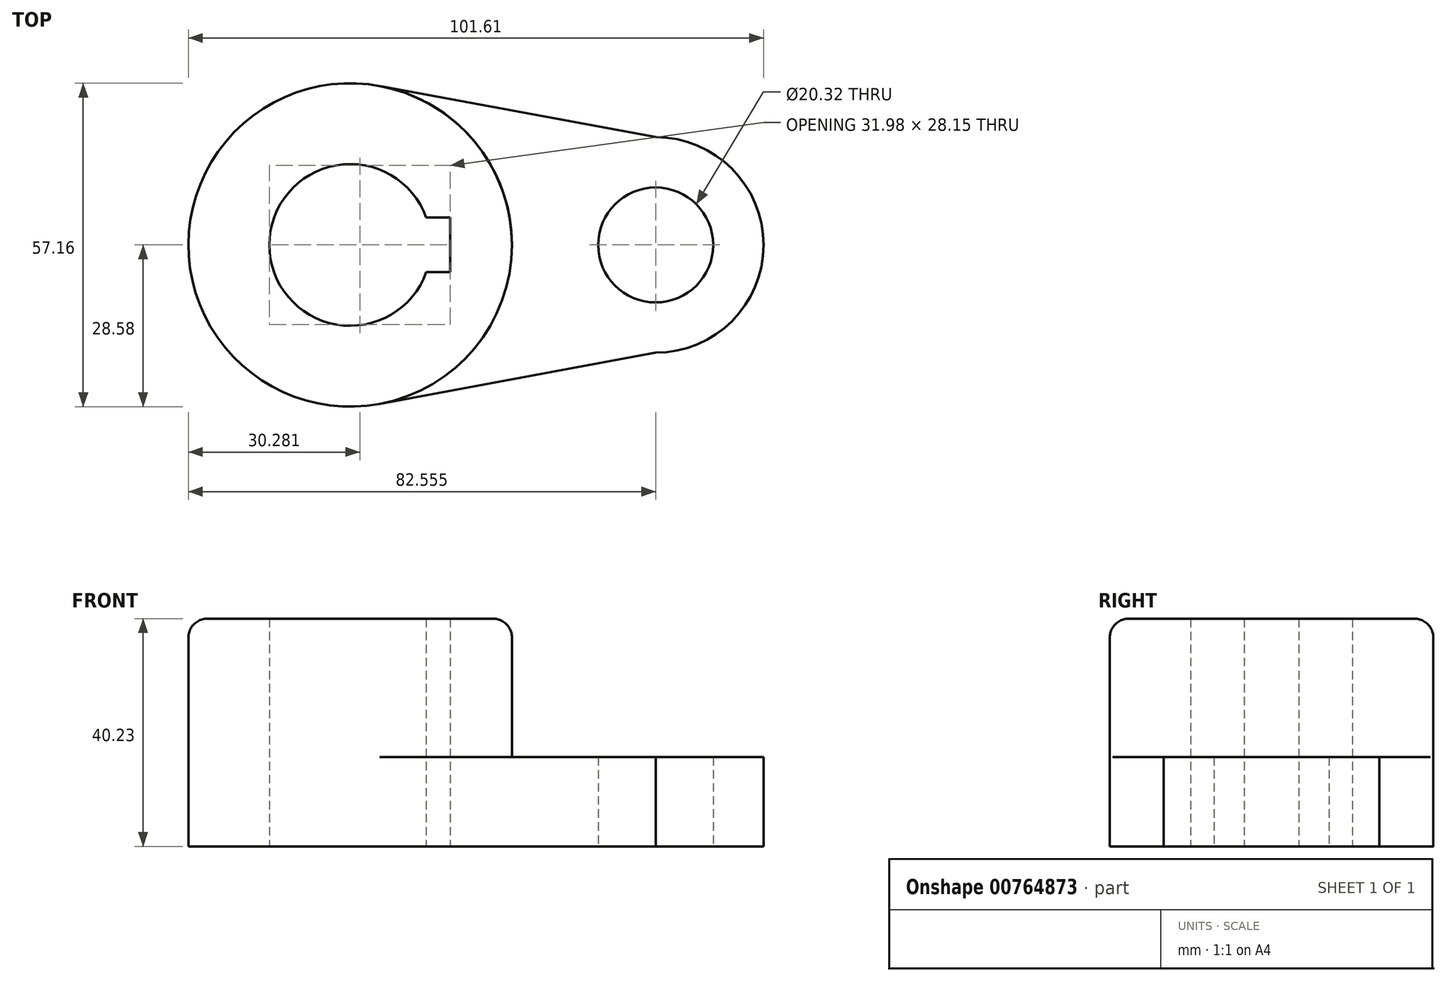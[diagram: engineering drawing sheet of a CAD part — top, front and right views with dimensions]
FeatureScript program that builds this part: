
annotation { "Feature Type Name" : "Feature", "Feature Type Description" : "" }
export const myFeature = defineFeature(function(context is Context, id is Id, definition is map)
    precondition{}
    {
        {
            var Q0;
            Q0=qCreatedBy(makeId("Top.planeOp"),FACE);
            var sketch = newSketch(context, id + "F0", { "sketchPlane" : qUnion([Q0])});
            skCircle(sketch, "E0", {"center": v(0, 0) * mm, "radius": 28.58 * mm});
            skArc(sketch, "E1", {"start": v(13.45, 4.83) * mm, "mid": v(-14.29, 0) * mm, "end": v(13.45, -4.83) * mm});
            skCircle(sketch, "E2", {"center": v(53.98, 0) * mm, "radius": 10.16 * mm});
            skLineSegment(sketch, "E3", {"start": v(13.45, -4.83) * mm, "end": v(17.69, -4.83) * mm});
            skLineSegment(sketch, "E4", {"start": v(17.69, -4.83) * mm, "end": v(13.45, -4.83) * mm});
            skLineSegment(sketch, "E5", {"start": v(17.69, -4.83) * mm, "end": v(17.69, 4.83) * mm});
            skLineSegment(sketch, "E6", {"start": v(17.69, 4.83) * mm, "end": v(13.45, 4.83) * mm});
            skCircle(sketch, "E7", {"center": v(53.98, 0) * mm, "radius": 19.05 * mm});
            skLineSegment(sketch, "E8", {"start": v(53.97, -19.05) * mm, "end": v(0, -29.06) * mm});
            skLineSegment(sketch, "E9", {"start": v(53.98, 19.05) * mm, "end": v(0, 29.06) * mm});
            skLineSegment(sketch, "E10", {"start": v(0, 29.06) * mm, "end": v(53.98, 19.05) * mm});
            skSolve(sketch);
        }
        {
            var Q0;
            {var subQ0=sQuery(id+"F0.wireOp",EDGE,"E8");var subQ1=sQuery(id+"F0.wireOp",EDGE,"E0");var subQ2=makeQuery(id+"F0.imprint","INTERSECT",VERTEX,{"derivedFrom":[subQ1,subQ0]});Q0=makeQuery(id+"F0.imprint","IMPRINT",FACE,{"disambiguationData":[TD([[makeQuery(id+"F0.imprint","IMPRINT",EDGE,{"disambiguationData":[TD([[subQ2,-1.0]])],"derivedFrom":subQ1}),-1.0]])]});}
            var Q1;
            Q1=makeQuery(id+"F0.imprint","IMPRINT",FACE,{"disambiguationData":[TD([[makeQuery(id+"F0.imprint","IMPRINT",EDGE,{"derivedFrom":sQuery(id+"F0.wireOp",EDGE,"E2")}),-1.0]])]});
            extrude(context, id + "F1", {"entities" : qUnion([Q0, Q1]), "depth" : 15.77 * mm, "offsetDistance" : 25.4 * mm});
        }
        {
            var Q0;
            Q0=makeQuery(id+"F0.imprint","IMPRINT",FACE,{"disambiguationData":[TD([[makeQuery(id+"F0.imprint","IMPRINT",EDGE,{"derivedFrom":sQuery(id+"F0.wireOp",EDGE,"E1")}),-1.0]])]});
            var sketch = newSketch(context, id + "F2", { "sketchPlane" : qUnion([Q0])});
            skSolve(sketch);
        }
        {
            var Q0;
            Q0=makeQuery(id+"F2.imprint","IMPRINT",FACE,{"disambiguationData":[TD([[makeQuery(id+"F2.imprint","IMPRINT",EDGE,{"derivedFrom":makeQuery(id+"F0.imprint","IMPRINT",EDGE,{"derivedFrom":sQuery(id+"F0.wireOp",EDGE,"E1")})}),-1.0]])]});
            extrude(context, id + "F3", {"entities" : qUnion([Q0]), "operationType" : NewBodyOperationType.ADD, "depth" : 40.23 * mm, "offsetDistance" : 25.4 * mm});
        }
        {
            var Q0;
            Q0=makeQuery(id+"F3.opExtrude","CAP_EDGE",EDGE,{"disambiguationData":[OSD([sQuery(id+"F0.wireOp",EDGE,"E0")])],"isStart":false});
            fillet(context, id + "F4", {"entities" : qUnion([Q0]), "radius" : 3.3 * mm, "tangentPropagation" : true, "allowEdgeOverflow" : false});
        }
    });
